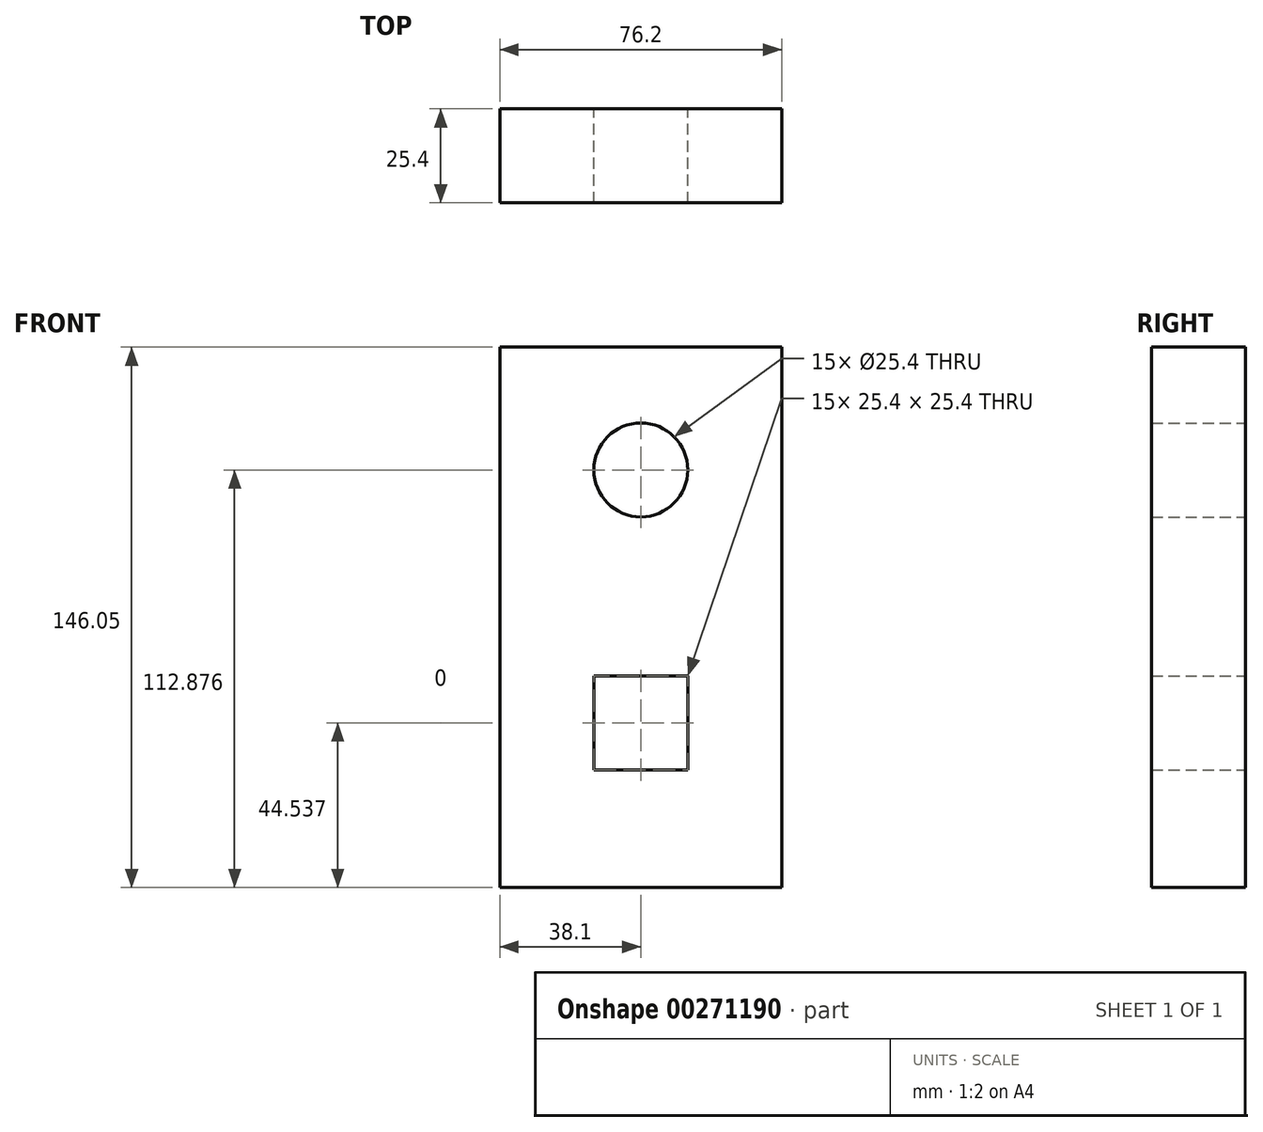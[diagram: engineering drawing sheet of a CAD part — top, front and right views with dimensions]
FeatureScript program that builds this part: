
annotation { "Feature Type Name" : "Feature", "Feature Type Description" : "" }
export const myFeature = defineFeature(function(context is Context, id is Id, definition is map)
    precondition{}
    {
        {
            var Q0;
            Q0=qCreatedBy(makeId("Front.planeOp"),FACE);
            var sketch = newSketch(context, id + "F0", { "sketchPlane" : qUnion([Q0])});
            skLineSegment(sketch, "E0.bottom", {"start": v(0, 0) * mm, "end": v(-76.2, 0) * mm});
            skLineSegment(sketch, "E0.top", {"start": v(0, 146.05) * mm, "end": v(-76.2, 146.05) * mm});
            skLineSegment(sketch, "E0.left", {"start": v(0, 0) * mm, "end": v(0, 146.05) * mm});
            skLineSegment(sketch, "E0.right", {"start": v(-76.2, 0) * mm, "end": v(-76.2, 146.05) * mm});
            skCircle(sketch, "E1", {"center": v(-38.1, 112.88) * mm, "radius": 12.7 * mm});
            skLineSegment(sketch, "E2.bottom", {"start": v(-25.4, 31.84) * mm, "end": v(-50.8, 31.84) * mm});
            skLineSegment(sketch, "E2.top", {"start": v(-25.4, 57.24) * mm, "end": v(-50.8, 57.24) * mm});
            skLineSegment(sketch, "E2.left", {"start": v(-25.4, 31.84) * mm, "end": v(-25.4, 57.24) * mm});
            skLineSegment(sketch, "E2.right", {"start": v(-50.8, 31.84) * mm, "end": v(-50.8, 57.24) * mm});
            skSolve(sketch);
        }
        {
            var Q0;
            Q0 = qSketchRegion(id + "F0", true);
            extrude(context, id + "F1", {"entities" : qUnion([Q0]), "depth" : 25.4 * mm});
        }
    });
